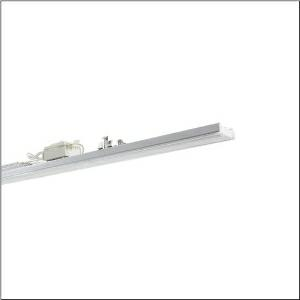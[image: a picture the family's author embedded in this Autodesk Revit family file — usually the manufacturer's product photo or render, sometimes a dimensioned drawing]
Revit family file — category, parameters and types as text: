
# Revit family: licross_11_recessed_mo_51te12dv4fxg3s
name_source: partatom
category: Lighting Fixtures
units: mm (PartAtom-declared; Revit-internal decimal feet)

## family parameters
Cut with Voids When Loaded = No
Host = Face
Light Source = No
Part Type = Normal
Room Calculation Point = No
Round Connector Dimension = Use Diameter
Shared = No

## types (1)
- --- (1 x LED, 1010 lm, 5.5 W, 4000K)
    Apparent Load = 6 VA
    CIE Flux Codes = 67 92 99 100 100
    Color Rendering = 80
    Color Temperature = 4000K
    Default Elevation = 1800 mm
    Description = Licross 11 Recessed MO, luminaire insert, of sheet steel, galvanised, coil coated, white, length: 2.250mm, width: 66mm, height: 67mm, LED rated luminous flux: 15.360lm, light colour: 840, SDCM (Standard Deviation of Colour Matching)MacAdam ≤ 2 SDCM (initial), control gear: DALI 2 (for two DALI lines), with plug, 6-pole, with phase selection, for trunking rail, 14-core, mains connection: 220..240V, AC, 50/60Hz, rated input power: 88W, for trunking rail, 14-core, internal wiring halogen-free, for emergency light function, converter,control gear: single battery element, battery: LiFePO4, 9Ah, primary optical cover: cover, of PMMA, light emission: direct distribution, primary light characteristic: symmetric, protection rating (complete): IP54, insulation class (complete): insulation class I (protective earthing), certification: CE, UKCA, protection symbol: D if used in an environment with non-conductive dust loads with corresponding accessories, impact resistance: IK06, permissible ambient temperature for indoor applications: +5..+35°C, standard: EN 60598-2-22, LABS conformity tested according to VDMA 24364:2018-05, reducing of maximum allowable ambient temperature of 5°C with ceiling mounting, corresponds to IFS (International Featured Standards) requirements for safety and quality in the food industry, The light source and the operating device comply with the requirements of the Ecodesign Regulation (EU) 2019/2020 and are replaceable in accordance with this regulation, packaging unit: 1 piece
    Height = 58 mm
    Lamp = 1 x LED
    Lamp Light Flux = 1010 lm
    Lamp Power = 5.5 W
    Lamp count = 1
    Length = 2250 mm
    Luminous efficacy = 184 lm/W
    Manufacturer = Siteco
    ModVariant = No
    Model = 51TE12DV4FXG3S
    Mounting Place = Ceiling
    Mounting Type = Pendant
    Number of Poles = 1
    OnlyDefault = Yes
    Power Factor = 1
    Product Name = Licross 11 Recessed MO
    Product group = luminaire insert | ceiling pendant
    ProductGroupID = 901
    Protection Class = Protection class I
    Protection Degree = IP 54
    RLX_Detail_Level = 1
    RLX_Emergency_Light_Flux = 0 lm
    RLX_Emergency_Type = 0
    RLX_Emergency_Type_DB = No
    RlxData = <blob elided: 30133 chars, md5=d7620df1>
    Socket = socket
    Standby Power = 0 W
    System Light Flux = 1010 lm
    System Power = 6 W
    Type Comments = : emergency light operation: 3 h
    Type Image = l_1296930.jpg
    URL = http://relux.com
    VarID = @adj_090023
    Voltage = 0 V
    Weight = 0.00 kg
    Width = 66 mm

## geometry (parser evidence)
native form markers: Blend x4, Sweep x9
no freeform markers — native parametric forms only
